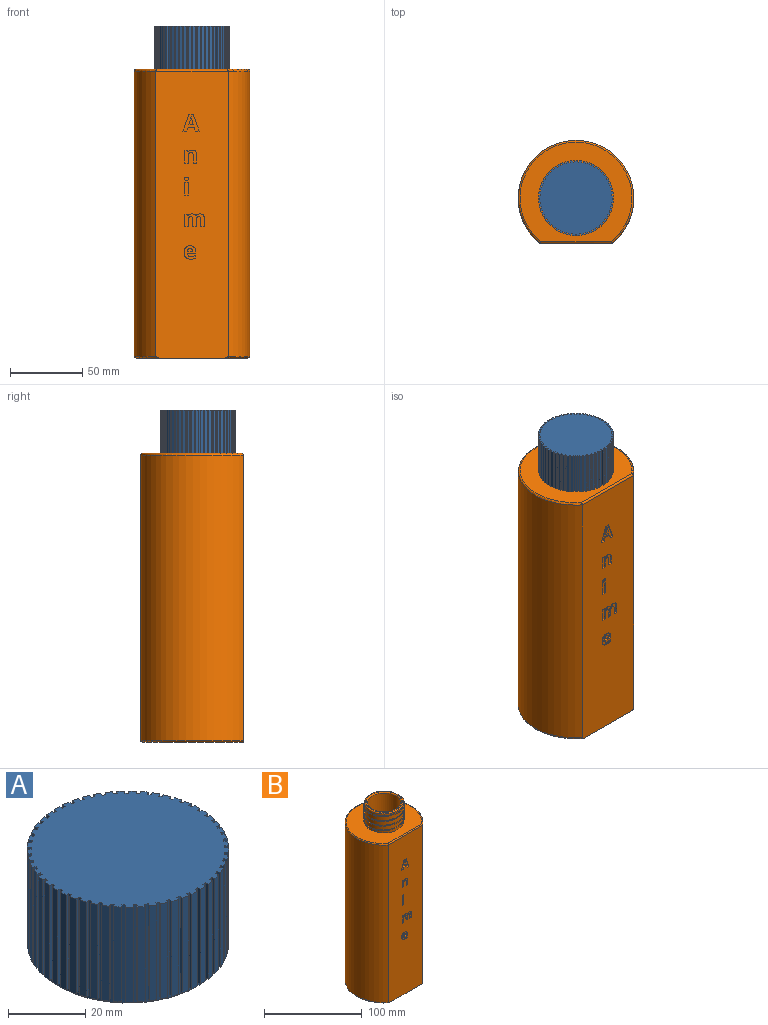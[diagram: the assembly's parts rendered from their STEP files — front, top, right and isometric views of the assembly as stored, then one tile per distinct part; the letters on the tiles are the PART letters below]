
ASSEMBLY  parts=2 mates=1
PART A: 222 faces, bbox 52.2x52.2x31.8 mm
  f0: plane 42.23x42.23mm, normal (0,0,-1), area 1381.8mm2, adj f4,f217,f218,f219
  f1: cylinder r=25mm len=50mm, axis (0,0,-1), area 1688.7mm2, adj f2,f3,f5,f6,f8,f9,f10,f12
  f2: plane 52x51.98mm, normal (0,0,1), area 2068.3mm2, adj f1,f5,f6,f7,f9,f10,f11,f13
  f3: plane 50x50mm, normal (0,0,-1), area 578.1mm2, adj f1,f4
  f4: cylinder r=21mm len=42mm, axis (0,0,-1), area 3562.6mm2, adj f0,f3
  f5: plane 30x1mm, normal (-1,0,0), area 30mm2, adj f1,f2,f7,f8
  f6: plane 30x1mm, normal (1,0,0), area 30mm2, adj f1,f2,f7,f8
  f7: plane 30x2mm, normal (0,1,0), area 60mm2, adj f2,f5,f6,f8
  f8: plane 2x1mm, normal (0,0,-1), area 2mm2, adj f1,f5,f6,f7
  f9: plane 30x0.99mm, normal (-0.99,0.12,0), area 30mm2, adj f1,f2,f11,f12
  f10: plane 30x1mm, normal (0.99,-0.12,0), area 30mm2, adj f1,f2,f11,f12
  f11: plane 30x1.99mm, normal (0.12,0.99,0), area 60mm2, adj f2,f9,f10,f12
  f12: plane 2.11x1.23mm, normal (0,0,-1), area 2mm2, adj f1,f9,f10,f11
  f13: plane 30x0.97mm, normal (-0.97,0.23,0), area 30mm2, adj f1,f2,f15,f16
  f14: plane 30x0.98mm, normal (0.97,-0.23,0), area 30mm2, adj f1,f2,f15,f16
  f15: plane 30x1.94mm, normal (0.23,0.97,0), area 60mm2, adj f2,f13,f14,f16
  f16: plane 2.18x1.45mm, normal (0,0,-1), area 2mm2, adj f1,f13,f14,f15
  f17: plane 30x0.94mm, normal (-0.94,0.35,0), area 30mm2, adj f1,f2,f19,f20
  f18: plane 30x0.94mm, normal (0.94,-0.35,0), area 30mm2, adj f1,f2,f19,f20
  f19: plane 30x1.88mm, normal (0.35,0.94,0), area 60mm2, adj f2,f17,f18,f20
  f20: plane 2.23x1.64mm, normal (0,0,-1), area 2mm2, adj f1,f17,f18,f19
  f21: plane 30x0.89mm, normal (-0.89,0.46,0), area 30mm2, adj f1,f2,f23,f24
  f22: plane 30x0.89mm, normal (0.89,-0.46,0), area 30mm2, adj f1,f2,f23,f24
  f23: plane 30x1.78mm, normal (0.46,0.89,0), area 60mm2, adj f2,f21,f22,f24
  f24: plane 2.24x1.81mm, normal (0,0,-1), area 2mm2, adj f1,f21,f22,f23
  f25: plane 30x0.83mm, normal (-0.83,0.56,0), area 30mm2, adj f1,f2,f27,f28
  f26: plane 30x0.83mm, normal (0.83,-0.56,0), area 30mm2, adj f1,f2,f27,f28
  f27: plane 30x1.66mm, normal (0.56,0.83,0), area 60mm2, adj f2,f25,f26,f28
  f28: plane 2.22x1.95mm, normal (0,0,-1), area 2mm2, adj f1,f25,f26,f27
  f29: plane 30x0.76mm, normal (-0.76,0.65,0), area 30mm2, adj f1,f2,f31,f32
  f30: plane 30x0.76mm, normal (0.76,-0.65,0), area 30mm2, adj f1,f2,f31,f32
  f31: plane 30x1.52mm, normal (0.65,0.76,0), area 60mm2, adj f2,f29,f30,f32
  f32: plane 2.17x2.07mm, normal (0,0,-1), area 2mm2, adj f1,f29,f30,f31
  f33: plane 30x0.74mm, normal (-0.67,0.74,0), area 30mm2, adj f1,f2,f35,f36
  f34: plane 30x0.74mm, normal (0.67,-0.74,0), area 30mm2, adj f1,f2,f35,f36
  f35: plane 30x1.48mm, normal (0.74,0.67,0), area 60mm2, adj f2,f33,f34,f36
  f36: plane 2.15x2.09mm, normal (0,0,-1), area 2mm2, adj f1,f33,f34,f35
  f37: plane 30x0.81mm, normal (-0.58,0.81,0), area 30mm2, adj f1,f2,f39,f40
  f38: plane 30x0.82mm, normal (0.58,-0.81,0), area 30mm2, adj f1,f2,f39,f40
  f39: plane 30x1.63mm, normal (0.81,0.58,0), area 60mm2, adj f2,f37,f38,f40
  f40: plane 2.21x1.98mm, normal (0,0,-1), area 2mm2, adj f1,f37,f38,f39
  f41: plane 30x0.88mm, normal (-0.48,0.88,0), area 30mm2, adj f1,f2,f43,f44
  f42: plane 30x0.88mm, normal (0.48,-0.88,0), area 30mm2, adj f1,f2,f43,f44
  f43: plane 30x1.75mm, normal (0.88,0.48,0), area 60mm2, adj f2,f41,f42,f44
  f44: plane 2.24x1.84mm, normal (0,0,-1), area 2mm2, adj f1,f41,f42,f43
  f45: plane 30x0.93mm, normal (-0.38,0.93,0), area 30mm2, adj f1,f2,f47,f48
  f46: plane 30x0.93mm, normal (0.38,-0.93,0), area 30mm2, adj f1,f2,f47,f48
  f47: plane 30x1.85mm, normal (0.93,0.38,0), area 60mm2, adj f2,f45,f46,f48
  f48: plane 2.23x1.68mm, normal (0,0,-1), area 2mm2, adj f1,f45,f46,f47
  f49: plane 30x0.96mm, normal (-0.26,0.96,0), area 30mm2, adj f1,f2,f51,f52
  f50: plane 30x0.97mm, normal (0.26,-0.96,0), area 30mm2, adj f1,f2,f51,f52
  f51: plane 30x1.93mm, normal (0.96,0.26,0), area 60mm2, adj f2,f49,f50,f52
  f52: plane 2.2x1.49mm, normal (0,0,-1), area 2mm2, adj f1,f49,f50,f51
  f53: plane 30x0.99mm, normal (-0.15,0.99,0), area 30mm2, adj f1,f2,f55,f56
  f54: plane 30x0.99mm, normal (0.15,-0.99,0), area 30mm2, adj f1,f2,f55,f56
  f55: plane 30x1.98mm, normal (0.99,0.15,0), area 60mm2, adj f2,f53,f54,f56
  f56: plane 2.13x1.29mm, normal (0,0,-1), area 2mm2, adj f1,f53,f54,f55
  f57: plane 30x1mm, normal (-0.03,1,0), area 30mm2, adj f1,f2,f59,f60
  f58: plane 30x1mm, normal (0.03,-1,0), area 30mm2, adj f1,f2,f59,f60
  f59: plane 30x2mm, normal (1,0.03,0), area 60mm2, adj f2,f57,f58,f60
  f60: plane 2.03x1.06mm, normal (0,0,-1), area 2mm2, adj f1,f57,f58,f59
  f61: plane 30x1mm, normal (0.09,1,0), area 30mm2, adj f1,f2,f63,f64
  f62: plane 30x1mm, normal (-0.09,-1,0), area 30mm2, adj f1,f2,f63,f64
  f63: plane 30x1.99mm, normal (1,-0.09,0), area 60mm2, adj f2,f61,f62,f64
  f64: plane 2.08x1.18mm, normal (0,0,-1), area 2mm2, adj f1,f61,f62,f63
  f65: plane 30x0.98mm, normal (0.21,0.98,0), area 30mm2, adj f1,f2,f67,f68
  f66: plane 30x0.98mm, normal (-0.21,-0.98,0), area 30mm2, adj f1,f2,f67,f68
  f67: plane 30x1.96mm, normal (0.98,-0.21,0), area 60mm2, adj f2,f65,f66,f68
  f68: plane 2.17x1.39mm, normal (0,0,-1), area 2mm2, adj f1,f65,f66,f67
  f69: plane 30x0.95mm, normal (0.32,0.95,0), area 30mm2, adj f1,f2,f71,f72
  f70: plane 30x0.95mm, normal (-0.32,-0.95,0), area 30mm2, adj f1,f2,f71,f72
  f71: plane 30x1.89mm, normal (0.95,-0.32,0), area 60mm2, adj f2,f69,f70,f72
  f72: plane 2.22x1.59mm, normal (0,0,-1), area 2mm2, adj f1,f69,f70,f71
  f73: plane 30x0.9mm, normal (0.43,0.9,0), area 30mm2, adj f1,f2,f75,f76
  f74: plane 30x0.91mm, normal (-0.43,-0.9,0), area 30mm2, adj f1,f2,f75,f76
  f75: plane 30x1.81mm, normal (0.9,-0.43,0), area 60mm2, adj f2,f73,f74,f76
  f76: plane 2.24x1.77mm, normal (0,0,-1), area 2mm2, adj f1,f73,f74,f75
  f77: plane 30x0.85mm, normal (0.53,0.85,0), area 30mm2, adj f1,f2,f79,f80
  f78: plane 30x0.85mm, normal (-0.53,-0.85,0), area 30mm2, adj f1,f2,f79,f80
  f79: plane 30x1.69mm, normal (0.85,-0.53,0), area 60mm2, adj f2,f77,f78,f80
  f80: plane 2.23x1.92mm, normal (0,0,-1), area 2mm2, adj f1,f77,f78,f79
  f81: plane 30x0.78mm, normal (0.63,0.78,0), area 30mm2, adj f1,f2,f83,f84
  f82: plane 30x0.78mm, normal (-0.63,-0.78,0), area 30mm2, adj f1,f2,f83,f84
  f83: plane 30x1.55mm, normal (0.78,-0.63,0), area 60mm2, adj f2,f81,f82,f84
  f84: plane 2.19x2.04mm, normal (0,0,-1), area 2mm2, adj f1,f81,f82,f83
  f85: plane 30x0.72mm, normal (0.72,0.7,0), area 30mm2, adj f1,f2,f87,f88
  f86: plane 30x0.72mm, normal (-0.72,-0.7,0), area 30mm2, adj f1,f2,f87,f88
  f87: plane 30x1.44mm, normal (0.7,-0.72,0), area 60mm2, adj f2,f85,f86,f88
  f88: plane 2.13x2.11mm, normal (0,0,-1), area 2mm2, adj f1,f85,f86,f87
  f89: plane 30x0.8mm, normal (0.79,0.61,0), area 30mm2, adj f1,f2,f91,f92
  f90: plane 30x0.8mm, normal (-0.79,-0.61,0), area 30mm2, adj f1,f2,f91,f92
  f91: plane 30x1.59mm, normal (0.61,-0.79,0), area 60mm2, adj f2,f89,f90,f92
  f92: plane 2.2x2.01mm, normal (0,0,-1), area 2mm2, adj f1,f89,f90,f91
  f93: plane 30x0.86mm, normal (0.86,0.51,0), area 30mm2, adj f1,f2,f95,f96
  f94: plane 30x0.86mm, normal (-0.86,-0.51,0), area 30mm2, adj f1,f2,f95,f96
  f95: plane 30x1.72mm, normal (0.51,-0.86,0), area 60mm2, adj f2,f93,f94,f96
  f96: plane 2.23x1.88mm, normal (0,0,-1), area 2mm2, adj f1,f93,f94,f95
  f97: plane 30x0.92mm, normal (0.92,0.4,0), area 30mm2, adj f1,f2,f99,f100
  f98: plane 30x0.92mm, normal (-0.92,-0.4,0), area 30mm2, adj f1,f2,f99,f100
  f99: plane 30x1.83mm, normal (0.4,-0.92,0), area 60mm2, adj f2,f97,f98,f100
  f100: plane 2.24x1.72mm, normal (0,0,-1), area 2mm2, adj f1,f97,f98,f99
  f101: plane 30x0.96mm, normal (0.96,0.29,0), area 30mm2, adj f1,f2,f103,f104
  f102: plane 30x0.96mm, normal (-0.96,-0.29,0), area 30mm2, adj f1,f2,f103,f104
  f103: plane 30x1.91mm, normal (0.29,-0.96,0), area 60mm2, adj f2,f101,f102,f104
  f104: plane 2.21x1.54mm, normal (0,0,-1), area 2mm2, adj f1,f101,f102,f103
  f105: plane 30x0.98mm, normal (0.98,0.18,0), area 30mm2, adj f1,f2,f107,f108
  f106: plane 30x0.99mm, normal (-0.98,-0.18,0), area 30mm2, adj f1,f2,f107,f108
  f107: plane 30x1.97mm, normal (0.18,-0.98,0), area 60mm2, adj f2,f105,f106,f108
  f108: plane 2.15x1.34mm, normal (0,0,-1), area 2mm2, adj f1,f105,f106,f107
  f109: plane 30x1mm, normal (1,0.06,0), area 30mm2, adj f1,f2,f111,f112
  f110: plane 30x1mm, normal (-1,-0.06,0), area 30mm2, adj f1,f2,f111,f112
  f111: plane 30x2mm, normal (0.06,-1,0), area 60mm2, adj f2,f109,f110,f112
  f112: plane 2.06x1.12mm, normal (0,0,-1), area 2mm2, adj f1,f109,f110,f111
  f113: plane 30x1mm, normal (1,-0.06,0), area 30mm2, adj f1,f2,f115,f116
  f114: plane 30x1mm, normal (-1,0.06,0), area 30mm2, adj f1,f2,f115,f116
  f115: plane 30x2mm, normal (-0.06,-1,0), area 60mm2, adj f2,f113,f114,f116
  f116: plane 2.06x1.12mm, normal (0,0,-1), area 2mm2, adj f1,f113,f114,f115
  f117: plane 30x0.98mm, normal (0.98,-0.18,0), area 30mm2, adj f1,f2,f119,f120
  f118: plane 30x0.99mm, normal (-0.98,0.18,0), area 30mm2, adj f1,f2,f119,f120
  f119: plane 30x1.97mm, normal (-0.18,-0.98,0), area 60mm2, adj f2,f117,f118,f120
  f120: plane 2.15x1.34mm, normal (0,0,-1), area 2mm2, adj f1,f117,f118,f119
  f121: plane 30x0.96mm, normal (0.96,-0.29,0), area 30mm2, adj f1,f2,f123,f124
  f122: plane 30x0.96mm, normal (-0.96,0.29,0), area 30mm2, adj f1,f2,f123,f124
  f123: plane 30x1.91mm, normal (-0.29,-0.96,0), area 60mm2, adj f2,f121,f122,f124
  f124: plane 2.21x1.54mm, normal (0,0,-1), area 2mm2, adj f1,f121,f122,f123
  f125: plane 30x0.92mm, normal (0.92,-0.4,0), area 30mm2, adj f1,f2,f127,f128
  f126: plane 30x0.92mm, normal (-0.92,0.4,0), area 30mm2, adj f1,f2,f127,f128
  f127: plane 30x1.83mm, normal (-0.4,-0.92,0), area 60mm2, adj f2,f125,f126,f128
  f128: plane 2.24x1.72mm, normal (0,0,-1), area 2mm2, adj f1,f125,f126,f127
  f129: plane 30x0.86mm, normal (0.86,-0.51,0), area 30mm2, adj f1,f2,f131,f132
  f130: plane 30x0.86mm, normal (-0.86,0.51,0), area 30mm2, adj f1,f2,f131,f132
  f131: plane 30x1.72mm, normal (-0.51,-0.86,0), area 60mm2, adj f2,f129,f130,f132
  f132: plane 2.23x1.88mm, normal (0,0,-1), area 2mm2, adj f1,f129,f130,f131
  f133: plane 30x0.8mm, normal (0.79,-0.61,0), area 30mm2, adj f1,f2,f135,f136
  f134: plane 30x0.8mm, normal (-0.79,0.61,0), area 30mm2, adj f1,f2,f135,f136
  f135: plane 30x1.59mm, normal (-0.61,-0.79,0), area 60mm2, adj f2,f133,f134,f136
  f136: plane 2.2x2.01mm, normal (0,0,-1), area 2mm2, adj f1,f133,f134,f135
  f137: plane 30x0.72mm, normal (0.72,-0.7,0), area 30mm2, adj f1,f2,f139,f140
  f138: plane 30x0.72mm, normal (-0.72,0.7,0), area 30mm2, adj f1,f2,f139,f140
  f139: plane 30x1.44mm, normal (-0.7,-0.72,0), area 60mm2, adj f2,f137,f138,f140
  f140: plane 2.13x2.11mm, normal (0,0,-1), area 2mm2, adj f1,f137,f138,f139
  f141: plane 30x0.78mm, normal (0.63,-0.78,0), area 30mm2, adj f1,f2,f143,f144
  f142: plane 30x0.78mm, normal (-0.63,0.78,0), area 30mm2, adj f1,f2,f143,f144
  f143: plane 30x1.55mm, normal (-0.78,-0.63,0), area 60mm2, adj f2,f141,f142,f144
  f144: plane 2.19x2.04mm, normal (0,0,-1), area 2mm2, adj f1,f141,f142,f143
  f145: plane 30x0.85mm, normal (0.53,-0.85,0), area 30mm2, adj f1,f2,f147,f148
  f146: plane 30x0.85mm, normal (-0.53,0.85,0), area 30mm2, adj f1,f2,f147,f148
  f147: plane 30x1.69mm, normal (-0.85,-0.53,0), area 60mm2, adj f2,f145,f146,f148
  f148: plane 2.23x1.92mm, normal (0,0,-1), area 2mm2, adj f1,f145,f146,f147
  f149: plane 30x0.9mm, normal (0.43,-0.9,0), area 30mm2, adj f1,f2,f151,f152
  f150: plane 30x0.91mm, normal (-0.43,0.9,0), area 30mm2, adj f1,f2,f151,f152
  f151: plane 30x1.81mm, normal (-0.9,-0.43,0), area 60mm2, adj f2,f149,f150,f152
  f152: plane 2.24x1.77mm, normal (0,0,-1), area 2mm2, adj f1,f149,f150,f151
  f153: plane 30x0.95mm, normal (0.32,-0.95,0), area 30mm2, adj f1,f2,f155,f156
  f154: plane 30x0.95mm, normal (-0.32,0.95,0), area 30mm2, adj f1,f2,f155,f156
  f155: plane 30x1.89mm, normal (-0.95,-0.32,0), area 60mm2, adj f2,f153,f154,f156
  f156: plane 2.22x1.59mm, normal (0,0,-1), area 2mm2, adj f1,f153,f154,f155
  f157: plane 30x0.98mm, normal (0.21,-0.98,0), area 30mm2, adj f1,f2,f159,f160
  f158: plane 30x0.98mm, normal (-0.21,0.98,0), area 30mm2, adj f1,f2,f159,f160
  f159: plane 30x1.96mm, normal (-0.98,-0.21,0), area 60mm2, adj f2,f157,f158,f160
  f160: plane 2.17x1.39mm, normal (0,0,-1), area 2mm2, adj f1,f157,f158,f159
  f161: plane 30x1mm, normal (0.09,-1,0), area 30mm2, adj f1,f2,f163,f164
  f162: plane 30x1mm, normal (-0.09,1,0), area 30mm2, adj f1,f2,f163,f164
  f163: plane 30x1.99mm, normal (-1,-0.09,0), area 60mm2, adj f2,f161,f162,f164
  f164: plane 2.08x1.18mm, normal (0,0,-1), area 2mm2, adj f1,f161,f162,f163
  f165: plane 30x1mm, normal (-0.03,-1,0), area 30mm2, adj f1,f2,f167,f168
  f166: plane 30x1mm, normal (0.03,1,0), area 30mm2, adj f1,f2,f167,f168
  f167: plane 30x2mm, normal (-1,0.03,0), area 60mm2, adj f2,f165,f166,f168
  f168: plane 2.03x1.06mm, normal (0,0,-1), area 2mm2, adj f1,f165,f166,f167
  f169: plane 30x0.99mm, normal (-0.15,-0.99,0), area 30mm2, adj f1,f2,f171,f172
  f170: plane 30x0.99mm, normal (0.15,0.99,0), area 30mm2, adj f1,f2,f171,f172
  f171: plane 30x1.98mm, normal (-0.99,0.15,0), area 60mm2, adj f2,f169,f170,f172
  f172: plane 2.13x1.29mm, normal (0,0,-1), area 2mm2, adj f1,f169,f170,f171
  f173: plane 30x0.96mm, normal (-0.26,-0.96,0), area 30mm2, adj f1,f2,f175,f176
  f174: plane 30x0.97mm, normal (0.26,0.96,0), area 30mm2, adj f1,f2,f175,f176
  f175: plane 30x1.93mm, normal (-0.96,0.26,0), area 60mm2, adj f2,f173,f174,f176
  f176: plane 2.2x1.5mm, normal (0,0,-1), area 2mm2, adj f1,f173,f174,f175
  f177: plane 30x0.93mm, normal (-0.38,-0.93,0), area 30mm2, adj f1,f2,f179,f180
  f178: plane 30x0.93mm, normal (0.38,0.93,0), area 30mm2, adj f1,f2,f179,f180
  f179: plane 30x1.85mm, normal (-0.93,0.38,0), area 60mm2, adj f2,f177,f178,f180
  f180: plane 2.23x1.68mm, normal (0,0,-1), area 2mm2, adj f1,f177,f178,f179
  f181: plane 30x0.88mm, normal (-0.48,-0.88,0), area 30mm2, adj f1,f2,f183,f184
  f182: plane 30x0.88mm, normal (0.48,0.88,0), area 30mm2, adj f1,f2,f183,f184
  f183: plane 30x1.75mm, normal (-0.88,0.48,0), area 60mm2, adj f2,f181,f182,f184
  f184: plane 2.24x1.84mm, normal (0,0,-1), area 2mm2, adj f1,f181,f182,f183
  f185: plane 30x0.81mm, normal (-0.58,-0.81,0), area 30mm2, adj f1,f2,f187,f188
  f186: plane 30x0.82mm, normal (0.58,0.81,0), area 30mm2, adj f1,f2,f187,f188
  f187: plane 30x1.63mm, normal (-0.81,0.58,0), area 60mm2, adj f2,f185,f186,f188
  f188: plane 2.21x1.98mm, normal (0,0,-1), area 2mm2, adj f1,f185,f186,f187
  f189: plane 30x0.74mm, normal (-0.67,-0.74,0), area 30mm2, adj f1,f2,f191,f192
  f190: plane 30x0.74mm, normal (0.67,0.74,0), area 30mm2, adj f1,f2,f191,f192
  f191: plane 30x1.48mm, normal (-0.74,0.67,0), area 60mm2, adj f2,f189,f190,f192
  f192: plane 2.15x2.09mm, normal (0,0,-1), area 2mm2, adj f1,f189,f190,f191
  f193: plane 30x0.76mm, normal (-0.76,-0.65,0), area 30mm2, adj f1,f2,f195,f196
  f194: plane 30x0.76mm, normal (0.76,0.65,0), area 30mm2, adj f1,f2,f195,f196
  f195: plane 30x1.52mm, normal (-0.65,0.76,0), area 60mm2, adj f2,f193,f194,f196
  f196: plane 2.17x2.07mm, normal (0,0,-1), area 2mm2, adj f1,f193,f194,f195
  f197: plane 30x0.83mm, normal (-0.83,-0.56,0), area 30mm2, adj f1,f2,f199,f200
  f198: plane 30x0.83mm, normal (0.83,0.56,0), area 30mm2, adj f1,f2,f199,f200
  f199: plane 30x1.66mm, normal (-0.56,0.83,0), area 60mm2, adj f2,f197,f198,f200
  f200: plane 2.22x1.95mm, normal (0,0,-1), area 2mm2, adj f1,f197,f198,f199
  f201: plane 30x0.89mm, normal (-0.89,-0.46,0), area 30mm2, adj f1,f2,f203,f204
  f202: plane 30x0.89mm, normal (0.89,0.46,0), area 30mm2, adj f1,f2,f203,f204
  f203: plane 30x1.78mm, normal (-0.46,0.89,0), area 60mm2, adj f2,f201,f202,f204
  f204: plane 2.24x1.81mm, normal (0,0,-1), area 2mm2, adj f1,f201,f202,f203
  f205: plane 30x0.94mm, normal (-0.94,-0.35,0), area 30mm2, adj f1,f2,f207,f208
  f206: plane 30x0.94mm, normal (0.94,0.35,0), area 30mm2, adj f1,f2,f207,f208
  f207: plane 30x1.88mm, normal (-0.35,0.94,0), area 60mm2, adj f2,f205,f206,f208
  f208: plane 2.23x1.64mm, normal (0,0,-1), area 2mm2, adj f1,f205,f206,f207
  f209: plane 30x0.97mm, normal (-0.97,-0.23,0), area 30mm2, adj f1,f2,f211,f212
  f210: plane 30x0.98mm, normal (0.97,0.23,0), area 30mm2, adj f1,f2,f211,f212
  f211: plane 30x1.94mm, normal (-0.23,0.97,0), area 60mm2, adj f2,f209,f210,f212
  f212: plane 2.18x1.44mm, normal (0,0,-1), area 2mm2, adj f1,f209,f210,f211
  f213: plane 30x0.99mm, normal (-0.99,-0.12,0), area 30mm2, adj f1,f2,f215,f216
  f214: plane 30x1mm, normal (0.99,0.12,0), area 30mm2, adj f1,f2,f215,f216
  f215: plane 30x1.99mm, normal (-0.12,0.99,0), area 60mm2, adj f2,f213,f214,f216
  f216: plane 2.11x1.23mm, normal (0,0,-1), area 2mm2, adj f1,f213,f214,f215
  f217: plane 0.87x0.58mm, normal (0,1,0), area 0.3mm2, adj f0,f219,f221
  f218: bspline ~48.26x41.8mm, area 509.8mm2, adj f0,f219,f220,f221
  f219: bspline ~48.26x41.8mm, area 522.8mm2, adj f0,f217,f218,f220,f221
  f220: plane 1x0.91mm, normal (0,-1,0), area 0.4mm2, adj f218,f219,f221
  f221: bspline ~48.06x41.62mm, area 513.6mm2, adj f217,f218,f219,f220
PART B: 120 faces, bbox 87.1x78.7x225.5 mm
  f0: plane 199.34x50.54mm, normal (0,-1,0), area 9667.5mm2, adj f1,f3,f18,f20,f21,f22,f23,f24
  f1: cylinder r=40mm len=197.6mm, axis (0,0,-1), area 38989.8mm2, adj f0,f18,f19
  f2: plane 77.83x69.05mm, normal (0,0,1), area 3172.6mm2, adj f8,f19,f20,f115,f116,f119
  f3: plane 77.6x70.03mm, normal (0,0,-1), area 4491.9mm2, adj f0,f18
  f4: cylinder r=20mm len=40mm, axis (0,0,-1), area 373.2mm2, adj f5,f17,f117
  f5: cylinder r=20mm len=40mm, axis (0,0,-1), area 747.2mm2, adj f4,f6,f16,f116,f117
  f6: cylinder r=20mm len=40mm, axis (0,0,-1), area 747.2mm2, adj f5,f7,f116,f117
  f7: cylinder r=20mm len=40mm, axis (0,0,-1), area 747.2mm2, adj f6,f8,f116,f117
  f8: cylinder r=20mm len=40mm, axis (0,0,-1), area 373.9mm2, adj f2,f7,f115,f116
  f9: plane 37.6x37.6mm, normal (0,0,1), area 69.7mm2, adj f15,f17
  f10: plane 194x47.85mm, normal (0,1,0), area 9282.4mm2, adj f11,f12,f13
  f11: cylinder r=37mm len=194mm, axis (0,0,-1), area 35006.9mm2, adj f10,f12,f13
  f12: plane 74x65.23mm, normal (0,0,-1), area 3105.6mm2, adj f10,f11,f14
  f13: plane 74x65.23mm, normal (0,0,1), area 4013.5mm2, adj f10,f11
  f14: cylinder r=17mm len=34mm, axis (0,0,-1), area 2862.6mm2, adj f12,f15
  f15: torus R=18.2mm, axis (0,0,1), area 206.5mm2, adj f9,f14
  f16: torus R=18.8mm, axis (0,0,1), area 0mm2, adj f5,f17,f116
  f17: torus R=18.8mm, axis (0,0,1), area 231.7mm2, adj f4,f9,f16,f117,f118
  f18: torus R=38.8mm, axis (0,0,1), area 370.8mm2, adj f0,f1,f3
  f19: torus R=38.8mm, axis (0,0,1), area 367.1mm2, adj f1,f2,f20
  f20: cylinder r=1.2mm len=50mm, axis (-1,0,0), area 93.4mm2, adj f0,f2,f19
  f21: plane 2.42x1mm, normal (0,0,1), area 2.4mm2, adj f0,f22,f37,f38
  f22: plane 5.79x1mm, normal (-1,0,0), area 5.8mm2, adj f0,f21,f23,f38
  f23: extruded ~2.42x1mm, area 2.6mm2, adj f0,f22,f24,f38
  f24: extruded ~2.35x1mm, area 2.6mm2, adj f0,f23,f25,f38
  f25: extruded ~1.62x1mm, area 1.7mm2, adj f0,f24,f26,f38
  f26: extruded ~1.12x1mm, area 1.5mm2, adj f0,f25,f27,f38
  f27: plane 1x0.13mm, normal (0,0,-1), area 0.1mm2, adj f0,f26,f28,f38
  f28: plane 1.14x1mm, normal (-0.96,0,-0.28), area 1.2mm2, adj f0,f27,f29,f38
  f29: plane 1.85x1mm, normal (0,0,-1), area 1.9mm2, adj f0,f28,f30,f38
  f30: plane 8.88x1mm, normal (1,0,0), area 8.9mm2, adj f0,f29,f31,f38
  f31: plane 2.42x1mm, normal (0,0,1), area 2.4mm2, adj f0,f30,f32,f38
  f32: plane 4.18x1mm, normal (-1,0,0), area 4.2mm2, adj f0,f31,f33,f38
  f33: extruded ~2.25x1mm, area 2.3mm2, adj f0,f32,f34,f38
  f34: extruded ~1.47x1mm, area 1.7mm2, adj f0,f33,f35,f38
  f35: extruded ~1.09x1mm, area 1.2mm2, adj f0,f34,f36,f38
  f36: extruded ~1.44x1mm, area 1.5mm2, adj f0,f35,f37,f38
  f37: plane 5.19x1mm, normal (1,0,0), area 5.2mm2, adj f0,f21,f36,f38
  f38: plane 9.05x8.2mm, normal (0,-1,0), area 48.2mm2, adj f21,f22,f23,f24,f25,f26,f27,f28
  f39: extruded ~4.25x1.31mm, area 4.4mm2, adj f40,f50,f51,f114
  f40: plane 3.03x1mm, normal (0,0,-1), area 3mm2, adj f39,f41,f51,f114
  f41: extruded ~5.03x1.5mm, area 5.2mm2, adj f40,f50,f51,f114
  f42: plane 2.77x1mm, normal (0.96,0,0.29), area 2.9mm2, adj f0,f43,f49,f51
  f43: plane 2.65x1mm, normal (0,0,1), area 2.7mm2, adj f0,f42,f44,f51
  f44: plane 11.66x4.12mm, normal (-0.94,0,-0.33), area 12.4mm2, adj f0,f43,f45,f51
  f45: plane 3.01x1mm, normal (0,0,-1), area 3mm2, adj f0,f44,f46,f51
  f46: plane 11.66x4.1mm, normal (0.94,0,-0.33), area 12.4mm2, adj f0,f45,f47,f51
  f47: plane 2.65x1mm, normal (0,0,1), area 2.7mm2, adj f0,f46,f48,f51
  f48: plane 2.77x1mm, normal (-0.96,0,0.29), area 2.9mm2, adj f0,f47,f49,f51
  f49: plane 4.24x1mm, normal (0,0,1), area 4.2mm2, adj f0,f42,f48,f51
  f50: extruded ~1x0.78mm, area 0.8mm2, adj f39,f41,f51,f114
  f51: plane 11.66x11.23mm, normal (0,-1,0), area 61.5mm2, adj f39,f40,f41,f42,f43,f44,f45,f46
  f52: plane 2.42x1mm, normal (0,0,1), area 2.4mm2, adj f0,f53,f79,f80
  f53: plane 4.46x1mm, normal (-1,0,0), area 4.5mm2, adj f0,f52,f54,f80
  f54: extruded ~2.02x1mm, area 2.1mm2, adj f0,f53,f55,f80
  f55: extruded ~1.33x1mm, area 1.5mm2, adj f0,f54,f56,f80
  f56: extruded ~1.01x1mm, area 1.2mm2, adj f0,f55,f57,f80
  f57: extruded ~1.44x1mm, area 1.5mm2, adj f0,f56,f58,f80
  f58: plane 5.19x1mm, normal (1,0,0), area 5.2mm2, adj f0,f57,f59,f80
  f59: plane 2.43x1mm, normal (0,0,1), area 2.4mm2, adj f0,f58,f60,f80
  f60: plane 5.79x1mm, normal (-1,0,0), area 5.8mm2, adj f0,f59,f61,f80
  f61: extruded ~2.48x1mm, area 2.7mm2, adj f0,f60,f62,f80
  f62: extruded ~2.28x1mm, area 2.5mm2, adj f0,f61,f63,f80
  f63: extruded ~1.57x1mm, area 1.6mm2, adj f0,f62,f64,f80
  f64: extruded ~1.05x1mm, area 1.4mm2, adj f0,f63,f65,f80
  f65: plane 1x0.21mm, normal (0,0,-1), area 0.2mm2, adj f0,f64,f66,f80
  f66: extruded ~2.7x1.3mm, area 3.2mm2, adj f0,f65,f67,f80
  f67: extruded ~1.55x1mm, area 1.6mm2, adj f0,f66,f68,f80
  f68: extruded ~1.03x1mm, area 1.4mm2, adj f0,f67,f69,f80
  f69: plane 1x0.13mm, normal (0,0,-1), area 0.1mm2, adj f0,f68,f70,f80
  f70: plane 1.14x1mm, normal (-0.96,0,-0.28), area 1.2mm2, adj f0,f69,f71,f80
  f71: plane 1.85x1mm, normal (0,0,-1), area 1.9mm2, adj f0,f70,f72,f80
  f72: plane 8.88x1mm, normal (1,0,0), area 8.9mm2, adj f0,f71,f73,f80
  f73: plane 2.42x1mm, normal (0,0,1), area 2.4mm2, adj f0,f72,f74,f80
  f74: plane 4.18x1mm, normal (-1,0,0), area 4.2mm2, adj f0,f73,f75,f80
  f75: extruded ~2.25x1mm, area 2.3mm2, adj f0,f74,f76,f80
  f76: extruded ~1.35x1mm, area 1.6mm2, adj f0,f75,f77,f80
  f77: extruded ~1.01x1mm, area 1.2mm2, adj f0,f76,f78,f80
  f78: extruded ~1.44x1mm, area 1.5mm2, adj f0,f77,f79,f80
  f79: plane 5.19x1mm, normal (1,0,0), area 5.2mm2, adj f0,f52,f78,f80
  f80: plane 13.49x9.05mm, normal (0,-1,0), area 74.9mm2, adj f52,f53,f54,f55,f56,f57,f58,f59
  f81: plane 2.42x1mm, normal (0,0,1), area 2.4mm2, adj f0,f82,f84,f85
  f82: plane 8.88x1mm, normal (-1,0,0), area 8.9mm2, adj f0,f81,f83,f85
  f83: plane 2.42x1mm, normal (0,0,-1), area 2.4mm2, adj f0,f82,f84,f85
  f84: plane 8.88x1mm, normal (1,0,0), area 8.9mm2, adj f0,f81,f83,f85
  f85: plane 8.88x2.42mm, normal (0,-1,0), area 21.5mm2, adj f81,f82,f83,f84
  f86: extruded ~1.32x1.18mm, area 2mm2, adj f0,f87,f90,f91
  f87: extruded ~1.32x1.19mm, area 2mm2, adj f0,f86,f88,f91
  f88: extruded ~1x0.99mm, area 1.1mm2, adj f0,f87,f89,f91
  f89: extruded ~1x0.88mm, area 1mm2, adj f0,f88,f90,f91
  f90: extruded ~1.32x1.18mm, area 2mm2, adj f0,f86,f89,f91
  f91: plane 2.64x2.38mm, normal (0,-1,0), area 5.2mm2, adj f86,f87,f88,f89,f90
  f92: extruded ~3.35x1.18mm, area 3.6mm2, adj f0,f93,f111,f112
  f93: extruded ~1.76x1mm, area 1.8mm2, adj f0,f92,f94,f112
  f94: extruded ~1.36x1mm, area 1.4mm2, adj f0,f93,f95,f112
  f95: plane 1.88x1mm, normal (-1,0,0), area 1.9mm2, adj f0,f94,f96,f112
  f96: extruded ~1.49x1mm, area 1.6mm2, adj f0,f95,f97,f112
  f97: extruded ~1.52x1mm, area 1.5mm2, adj f0,f96,f98,f112
  f98: extruded ~1.6x1mm, area 1.8mm2, adj f0,f97,f99,f112
  f99: extruded ~1.61x1mm, area 1.8mm2, adj f0,f98,f100,f112
  f100: plane 5.73x1mm, normal (0,0,1), area 5.7mm2, adj f0,f99,f101,f112
  f101: plane 1.18x1mm, normal (-1,0,0), area 1.2mm2, adj f0,f100,f102,f112
  f102: extruded ~2.96x1.05mm, area 3.2mm2, adj f0,f101,f103,f112
  f103: extruded ~2.93x1.07mm, area 3.2mm2, adj f0,f102,f104,f112
  f104: extruded ~3.09x1.22mm, area 3.4mm2, adj f0,f103,f105,f112
  f105: extruded ~3.45x1.12mm, area 3.7mm2, adj f0,f104,f111,f112
  f106: extruded ~1.21x1mm, area 1.3mm2, adj f107,f110,f112,f113
  f107: extruded ~1.22x1mm, area 1.4mm2, adj f106,f108,f112,f113
  f108: extruded ~1.39x1mm, area 1.5mm2, adj f107,f109,f112,f113
  f109: plane 3.4x1mm, normal (0,0,-1), area 3.4mm2, adj f108,f110,f112,f113
  f110: extruded ~1.39x1mm, area 1.5mm2, adj f106,f109,f112,f113
  f111: extruded ~3.35x1.21mm, area 3.7mm2, adj f0,f92,f105,f112
  f112: plane 9.21x8.18mm, normal (0,-1,0), area 47.6mm2, adj f92,f93,f94,f95,f96,f97,f98,f99
  f113: plane 3.4x1.87mm, normal (0,-1,0), area 5.1mm2, adj f106,f107,f108,f109,f110
  f114: plane 5.03x3.03mm, normal (0,-1,0), area 7.5mm2, adj f39,f40,f41,f50
  f115: plane 0.9x0.42mm, normal (0,-1,0), area 0.2mm2, adj f2,f8,f116,f117,f119
  f116: bspline ~48.07x41.63mm, area 504.7mm2, adj f2,f5,f6,f7,f8,f16,f115,f118
  f117: bspline ~48.28x41.81mm, area 513.8mm2, adj f4,f5,f6,f7,f17,f115,f118,f119
  f118: plane 1x0.9mm, normal (0,1,0), area 0.4mm2, adj f17,f116,f117,f119
  f119: bspline ~48.28x41.81mm, area 520.2mm2, adj f2,f115,f116,f117,f118
PLACE A t=(22.41,60.48,167.96)mm
PLACE B t=(22.41,60.48,-31.1)mm
MATE cylindrical A.f1 <-> B.f4  axis (0,0,1) through (22.41,60.48,198.96)mm
